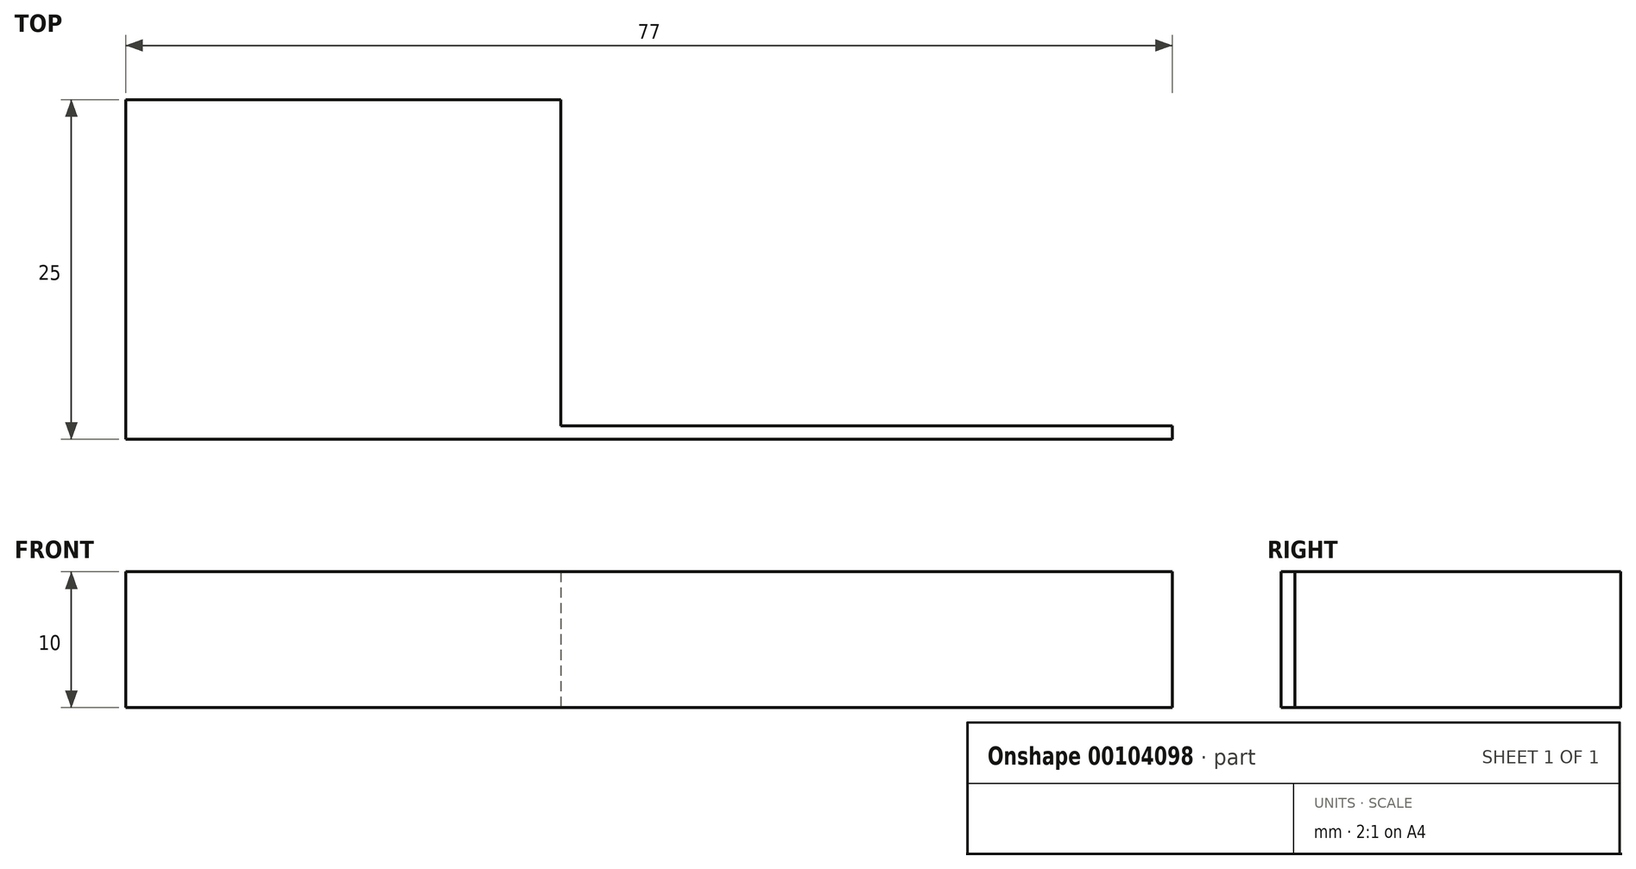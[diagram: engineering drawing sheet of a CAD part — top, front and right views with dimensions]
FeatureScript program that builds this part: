
annotation { "Feature Type Name" : "Feature", "Feature Type Description" : "" }
export const myFeature = defineFeature(function(context is Context, id is Id, definition is map)
    precondition{}
    {
        {
            var Q0;
            Q0=qCreatedBy(makeId("Front.planeOp"),FACE);
            var sketch = newSketch(context, id + "F0", { "sketchPlane" : qUnion([Q0])});
            skLineSegment(sketch, "E0.bottom", {"start": v(-32, 10) * mm, "end": v(0, 10) * mm});
            skLineSegment(sketch, "E0.top", {"start": v(-32, 0) * mm, "end": v(0, 0) * mm});
            skLineSegment(sketch, "E0.left", {"start": v(-32, 10) * mm, "end": v(-32, 0) * mm});
            skLineSegment(sketch, "E0.right", {"start": v(0, 10) * mm, "end": v(0, 0) * mm});
            skLineSegment(sketch, "E1.bottom", {"start": v(0, 10) * mm, "end": v(45, 10) * mm});
            skLineSegment(sketch, "E1.top", {"start": v(0, 0) * mm, "end": v(45, 0) * mm});
            skLineSegment(sketch, "E1.right", {"start": v(45, 10) * mm, "end": v(45, 0) * mm});
            skSolve(sketch);
        }
        {
            var Q0;
            Q0=makeQuery(id+"F0.imprint","IMPRINT",FACE,{"disambiguationData":[TD([[makeQuery(id+"F0.imprint","IMPRINT",EDGE,{"derivedFrom":sQuery(id+"F0.wireOp",EDGE,"E0.bottom")}),-1.0]])]});
            extrude(context, id + "F1", {"entities" : qUnion([Q0]), "oppositeDirection" : true, "depth" : 25 * mm});
        }
        {
            var Q0;
            Q0=makeQuery(id+"F0.imprint","IMPRINT",FACE,{"disambiguationData":[TD([[makeQuery(id+"F0.imprint","IMPRINT",EDGE,{"derivedFrom":sQuery(id+"F0.wireOp",EDGE,"E1.bottom")}),-1.0]])]});
            extrude(context, id + "F2", {"entities" : qUnion([Q0]), "operationType" : NewBodyOperationType.ADD, "oppositeDirection" : true, "depth" : 1 * mm});
        }
    });
